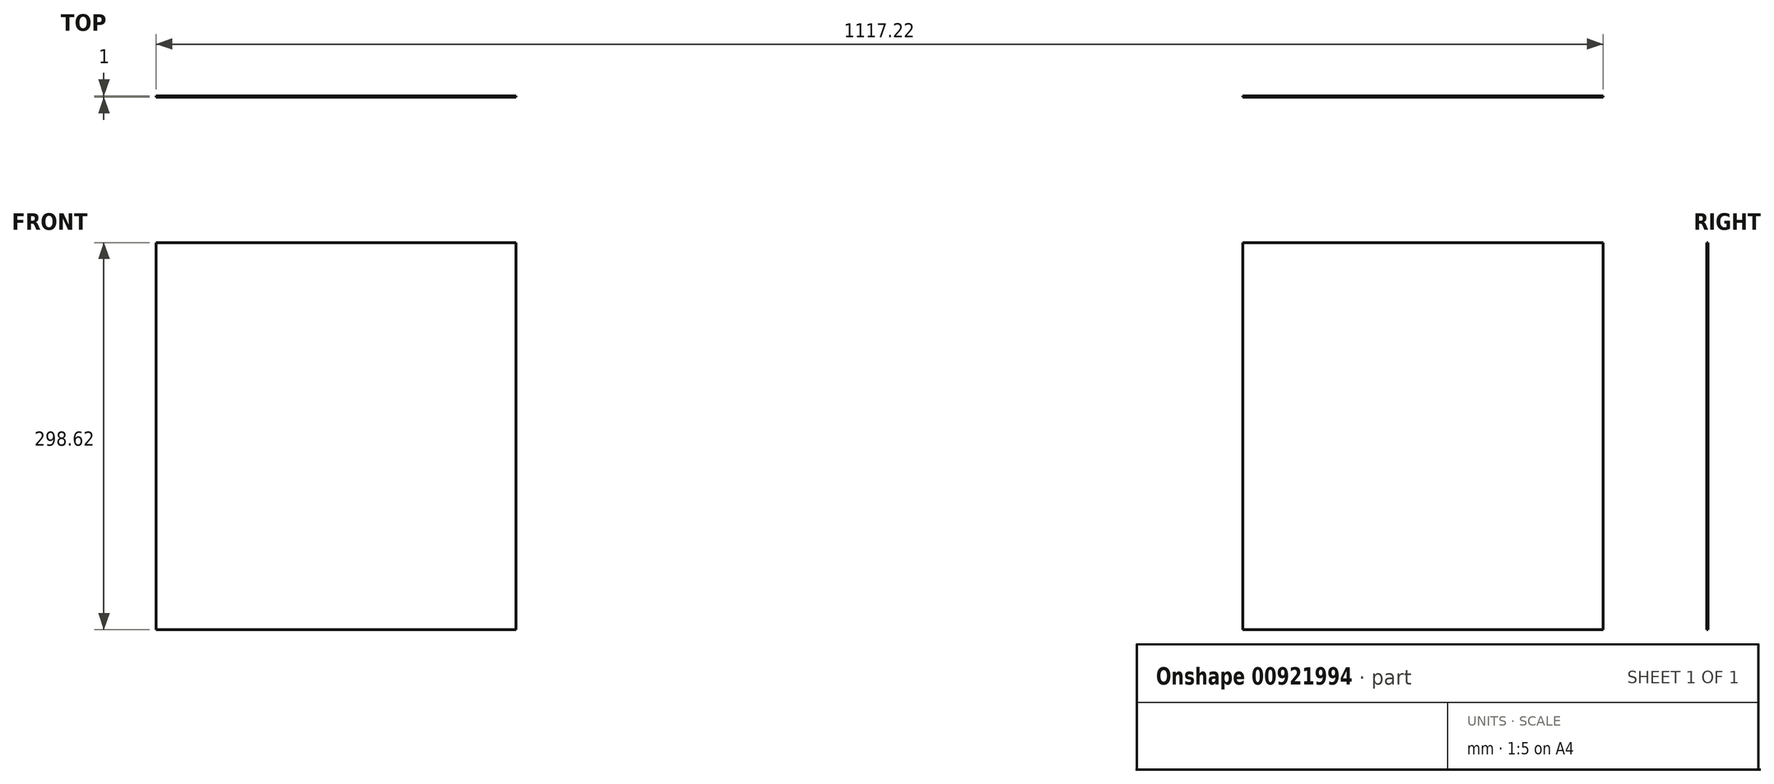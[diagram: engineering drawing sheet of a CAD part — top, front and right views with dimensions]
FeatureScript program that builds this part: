
annotation { "Feature Type Name" : "Feature", "Feature Type Description" : "" }
export const myFeature = defineFeature(function(context is Context, id is Id, definition is map)
    precondition{}
    {
        {
            var Q0;
            Q0=qCreatedBy(makeId("Front.planeOp"),FACE);
            cPlane(context, id + "F0", {"entities" : qUnion([Q0]), "cplaneType" : CPlaneType.OFFSET, "offset" : 15 * mm, "width" : 150 * mm, "height" : 150 * mm});
        }
        {
            var Q0;
            Q0=qCreatedBy(id+"F0.planeOp",FACE);
            var sketch = newSketch(context, id + "F1", { "sketchPlane" : qUnion([Q0])});
            skLineSegment(sketch, "E0.bottom", {"start": v(280.5, 334) * mm, "end": v(558.6, 334) * mm});
            skLineSegment(sketch, "E0.top", {"start": v(280.5, 35.38) * mm, "end": v(558.6, 35.38) * mm});
            skLineSegment(sketch, "E0.left", {"start": v(280.5, 334) * mm, "end": v(280.5, 35.38) * mm});
            skLineSegment(sketch, "E0.right", {"start": v(558.6, 334) * mm, "end": v(558.6, 35.38) * mm});
            skSolve(sketch);
        }
        {
            var Q0;
            Q0=makeQuery(id+"F1.imprint","IMPRINT",FACE,{"disambiguationData":[TD([[makeQuery(id+"F1.imprint","IMPRINT",EDGE,{"derivedFrom":sQuery(id+"F1.wireOp",EDGE,"E0.bottom")}),-1.0]])]});
            extrude(context, id + "F2", {"entities" : qUnion([Q0]), "depth" : 1 * mm, "offsetDistance" : 25 * mm});
        }
        {
            var Q0;
            Q0=makeQuery(id+"F2.opExtrude","SWEPT_BODY",BODY,{"disambiguationData":[OSD([sQuery(id+"F1.wireOp",EDGE,"E0.bottom"),sQuery(id+"F1.wireOp",EDGE,"E0.top"),sQuery(id+"F1.wireOp",EDGE,"E0.left"),sQuery(id+"F1.wireOp",EDGE,"E0.right")])]});
            var Q1;
            Q1=qCreatedBy(makeId("Right.planeOp"),FACE);
            mirror(context, id + "F3", {"entities" : qUnion([Q0]), "mirrorPlane" : qUnion([Q1])});
        }
    });
